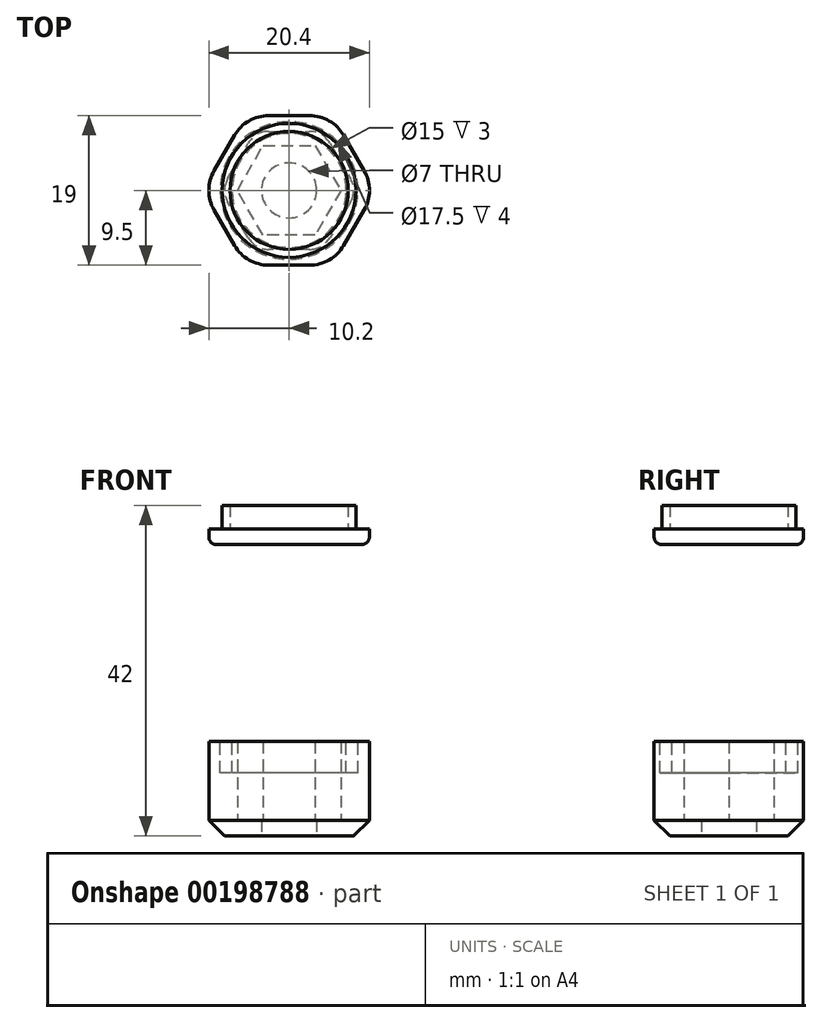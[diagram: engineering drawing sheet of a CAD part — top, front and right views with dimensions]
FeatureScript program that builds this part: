
annotation { "Feature Type Name" : "Feature", "Feature Type Description" : "" }
export const myFeature = defineFeature(function(context is Context, id is Id, definition is map)
    precondition{}
    {
        {
            var Q0;
            Q0=qCreatedBy(makeId("Top.planeOp"),FACE);
            var sketch = newSketch(context, id + "F0", { "sketchPlane" : qUnion([Q0])});
            skCircle(sketch, "E0.cCircle", {"center": v(0, 0) * mm, "radius": 5.7 * mm, "construction": true});
            skLineSegment(sketch, "E0.0", {"start": v(6.58, 0) * mm, "end": v(3.3, -5.7) * mm});
            skLineSegment(sketch, "E0.1", {"start": v(3.3, -5.7) * mm, "end": v(-3.3, -5.7) * mm});
            skLineSegment(sketch, "E0.2", {"start": v(-3.3, -5.7) * mm, "end": v(-6.58, 0) * mm});
            skLineSegment(sketch, "E0.3", {"start": v(-6.58, 0) * mm, "end": v(-3.3, 5.7) * mm});
            skLineSegment(sketch, "E0.4", {"start": v(-3.3, 5.7) * mm, "end": v(3.3, 5.7) * mm});
            skLineSegment(sketch, "E0.5", {"start": v(3.3, 5.7) * mm, "end": v(6.58, 0) * mm});
            skPoint(sketch, "E0.0.midPoint", {"position": v(4.94, -2.85) * mm});
            skCircle(sketch, "E1.cCircle", {"center": v(0, 0) * mm, "radius": 9.5 * mm, "construction": true});
            skLineSegment(sketch, "E1.0", {"start": v(-5.48, 9.5) * mm, "end": v(5.48, 9.5) * mm});
            skLineSegment(sketch, "E1.1", {"start": v(5.48, 9.5) * mm, "end": v(10.97, 0) * mm});
            skLineSegment(sketch, "E1.2", {"start": v(10.97, 0) * mm, "end": v(5.48, -9.5) * mm});
            skLineSegment(sketch, "E1.3", {"start": v(5.48, -9.5) * mm, "end": v(-5.48, -9.5) * mm});
            skLineSegment(sketch, "E1.4", {"start": v(-5.48, -9.5) * mm, "end": v(-10.97, 0) * mm});
            skLineSegment(sketch, "E1.5", {"start": v(-10.97, 0) * mm, "end": v(-5.48, 9.5) * mm});
            skPoint(sketch, "E1.0.midPoint", {"position": v(0, 9.5) * mm});
            skCircle(sketch, "E2", {"center": v(0, 0) * mm, "radius": 3.5 * mm});
            skSolve(sketch);
        }
        {
            var Q0;
            Q0 = qSketchRegion(id + "F0", true);
            extrude(context, id + "F1", {"entities" : qUnion([Q0]), "depth" : 12 * mm});
        }
        {
            var Q0;
            Q0=makeQuery(id+"F0.imprint","IMPRINT",FACE,{"disambiguationData":[TD([[makeQuery(id+"F0.imprint","IMPRINT",EDGE,{"derivedFrom":sQuery(id+"F0.wireOp",EDGE,"E0.0")}),-1.0]])]});
            extrude(context, id + "F2", {"entities" : qUnion([Q0]), "operationType" : NewBodyOperationType.ADD, "depth" : 2 * mm});
        }
        {
            var Q0;
            Q0=makeQuery(id+"F1.opExtrude","SWEPT_EDGE",EDGE,{"disambiguationData":[OSD([sQuery(id+"F0.wireOp",EDGE,"E1.0"),sQuery(id+"F0.wireOp",EDGE,"E1.5")])]});
            var Q1;
            Q1=makeQuery(id+"F1.opExtrude","SWEPT_EDGE",EDGE,{"disambiguationData":[OSD([sQuery(id+"F0.wireOp",EDGE,"E1.4"),sQuery(id+"F0.wireOp",EDGE,"E1.5")])]});
            var Q2;
            Q2=makeQuery(id+"F1.opExtrude","SWEPT_EDGE",EDGE,{"disambiguationData":[OSD([sQuery(id+"F0.wireOp",EDGE,"E1.3"),sQuery(id+"F0.wireOp",EDGE,"E1.4")])]});
            var Q3;
            Q3=makeQuery(id+"F1.opExtrude","SWEPT_EDGE",EDGE,{"disambiguationData":[OSD([sQuery(id+"F0.wireOp",EDGE,"E1.2"),sQuery(id+"F0.wireOp",EDGE,"E1.3")])]});
            var Q4;
            Q4=makeQuery(id+"F1.opExtrude","SWEPT_EDGE",EDGE,{"disambiguationData":[OSD([sQuery(id+"F0.wireOp",EDGE,"E1.1"),sQuery(id+"F0.wireOp",EDGE,"E1.2")])]});
            var Q5;
            Q5=makeQuery(id+"F1.opExtrude","SWEPT_EDGE",EDGE,{"disambiguationData":[OSD([sQuery(id+"F0.wireOp",EDGE,"E1.0"),sQuery(id+"F0.wireOp",EDGE,"E1.1")])]});
            fillet(context, id + "F3", {"entities" : qUnion([Q0, Q1, Q2, Q3, Q4, Q5]), "radius" : 5 * mm, "tangentPropagation" : true, "allowEdgeOverflow" : false});
        }
        {
            var Q0;
            Q0=makeQuery(id+"F1.opExtrude","CAP_FACE",FACE,{"disambiguationData":[OSD([sQuery(id+"F0.wireOp",EDGE,"E0.0"),sQuery(id+"F0.wireOp",EDGE,"E0.1"),sQuery(id+"F0.wireOp",EDGE,"E0.2"),sQuery(id+"F0.wireOp",EDGE,"E0.3"),sQuery(id+"F0.wireOp",EDGE,"E0.4"),sQuery(id+"F0.wireOp",EDGE,"E0.5"),sQuery(id+"F0.wireOp",EDGE,"E1.0"),sQuery(id+"F0.wireOp",EDGE,"E1.1"),sQuery(id+"F0.wireOp",EDGE,"E1.2"),sQuery(id+"F0.wireOp",EDGE,"E1.3"),sQuery(id+"F0.wireOp",EDGE,"E1.4"),sQuery(id+"F0.wireOp",EDGE,"E1.5")])],"isStart":false});
            var sketch = newSketch(context, id + "F4", { "sketchPlane" : qUnion([Q0])});
            skCircle(sketch, "E3", {"center": v(0, 0) * mm, "radius": 7.25 * mm});
            skCircle(sketch, "E4", {"center": v(0, 0) * mm, "radius": 8.75 * mm});
            skSolve(sketch);
        }
        {
            var Q0;
            Q0 = qSketchRegion(id + "F4", true);
            extrude(context, id + "F5", {"entities" : qUnion([Q0]), "operationType" : NewBodyOperationType.REMOVE, "oppositeDirection" : true, "depth" : 4 * mm});
        }
        {
            var Q0;
            {var subQ0=sQuery(id+"F0.wireOp",EDGE,"E1.3");var subQ1=sQuery(id+"F0.wireOp",EDGE,"E1.2");var subQ2=sQuery(id+"F0.wireOp",EDGE,"E1.1");var subQ3=sQuery(id+"F0.wireOp",EDGE,"E1.0");var subQ4=sQuery(id+"F0.wireOp",EDGE,"E1.5");var subQ5=sQuery(id+"F0.wireOp",EDGE,"E1.4");Q0=makeQuery(id+"F5.boolean.opBoolean","SPLIT",FACE,{"disambiguationData":[TD([makeQuery(id+"F1.opExtrude","SWEPT_FACE",FACE,{"disambiguationData":[OSD([subQ3])]})])],"derivedFrom":makeQuery(id+"F1.opExtrude","CAP_FACE",FACE,{"disambiguationData":[OSD([sQuery(id+"F0.wireOp",EDGE,"E0.0"),sQuery(id+"F0.wireOp",EDGE,"E0.1"),sQuery(id+"F0.wireOp",EDGE,"E0.2"),sQuery(id+"F0.wireOp",EDGE,"E0.3"),sQuery(id+"F0.wireOp",EDGE,"E0.4"),sQuery(id+"F0.wireOp",EDGE,"E0.5"),subQ3,subQ2,subQ1,subQ0,subQ5,subQ4])],"isStart":false})});}
            cPlane(context, id + "F6", {"entities" : qUnion([Q0]), "cplaneType" : CPlaneType.OFFSET, "offset" : 25 * mm, "width" : 150 * mm, "height" : 150 * mm});
        }
        {
            var Q0;
            Q0=qCreatedBy(id+"F6.planeOp",FACE);
            var sketch = newSketch(context, id + "F7", { "sketchPlane" : qUnion([Q0])});
            skPoint(sketch, "E5.0", {"position": v(10.2, 0) * mm});
            skLineSegment(sketch, "E6.0", {"start": v(-2.6, 9.5) * mm, "end": v(2.6, 9.5) * mm});
            skArc(sketch, "E7.0", {"start": v(6.93, 7) * mm, "mid": v(5.1, 8.83) * mm, "end": v(2.6, 9.5) * mm});
            skArc(sketch, "E8.0", {"start": v(-2.6, 9.5) * mm, "mid": v(-5.1, 8.83) * mm, "end": v(-6.93, 7) * mm});
            skCircle(sketch, "E9.0", {"center": v(0, 0) * mm, "radius": 9.5 * mm});
            skLineSegment(sketch, "E10.0", {"start": v(-8.23, 4.75) * mm, "end": v(-6.93, 7) * mm});
            skPoint(sketch, "E11.orphan", {"position": v(-10.97, 0) * mm});
            skPoint(sketch, "E12.orphan", {"position": v(-5.48, 9.5) * mm});
            skPoint(sketch, "E13.0.start.orphan", {"position": v(-5.48, -9.5) * mm});
            skPoint(sketch, "E14.0.start.orphan", {"position": v(5.48, -9.5) * mm});
            skPoint(sketch, "E15.0.start.orphan", {"position": v(10.97, 0) * mm});
            skPoint(sketch, "E16.0.start.orphan", {"position": v(5.48, 9.5) * mm});
            skArc(sketch, "E17.0", {"start": v(-9.53, 2.5) * mm, "mid": v(-10.2, 0) * mm, "end": v(-9.53, -2.5) * mm});
            skLineSegment(sketch, "E18.0", {"start": v(-9.53, 2.5) * mm, "end": v(-6.93, 7) * mm});
            skLineSegment(sketch, "E19.0", {"start": v(-6.93, -7) * mm, "end": v(-9.53, -2.5) * mm});
            skArc(sketch, "E20.0", {"start": v(-6.93, -7) * mm, "mid": v(-5.1, -8.83) * mm, "end": v(-2.6, -9.5) * mm});
            skLineSegment(sketch, "E21.0", {"start": v(2.6, -9.5) * mm, "end": v(-2.6, -9.5) * mm});
            skArc(sketch, "E22.0", {"start": v(2.6, -9.5) * mm, "mid": v(5.1, -8.83) * mm, "end": v(6.93, -7) * mm});
            skLineSegment(sketch, "E23.0", {"start": v(9.53, -2.5) * mm, "end": v(8.23, -4.75) * mm});
            skArc(sketch, "E24.0", {"start": v(9.53, -2.5) * mm, "mid": v(10.2, 0) * mm, "end": v(9.53, 2.5) * mm});
            skLineSegment(sketch, "E25.0", {"start": v(6.93, 7) * mm, "end": v(9.53, 2.5) * mm});
            skLineSegment(sketch, "E26.0", {"start": v(9.53, -2.5) * mm, "end": v(6.93, -7) * mm});
            skCircle(sketch, "E27", {"center": v(0, 0) * mm, "radius": 8.5 * mm});
            skCircle(sketch, "E28", {"center": v(0, 0) * mm, "radius": 7.5 * mm});
            skSolve(sketch);
        }
        {
            var Q0;
            Q0=makeQuery(id+"F7.imprint","IMPRINT",FACE,{"disambiguationData":[TD([[makeQuery(id+"F7.imprint","IMPRINT",EDGE,{"derivedFrom":sQuery(id+"F7.wireOp",EDGE,"E27")}),1.0]])]});
            extrude(context, id + "F8", {"entities" : qUnion([Q0]), "depth" : 5 * mm});
        }
        {
            var Q0;
            Q0=makeQuery(id+"F7.imprint","IMPRINT",FACE,{"disambiguationData":[TD([[makeQuery(id+"F7.imprint","IMPRINT",EDGE,{"derivedFrom":sQuery(id+"F7.wireOp",EDGE,"E27")}),1.0]])]});
            var Q1;
            Q1=makeQuery(id+"F7.imprint","IMPRINT",FACE,{"disambiguationData":[TD([[makeQuery(id+"F7.imprint","IMPRINT",EDGE,{"derivedFrom":sQuery(id+"F7.wireOp",EDGE,"E27")}),-1.0]])]});
            var Q2;
            {var subQ5=sQuery(id+"F7.wireOp",EDGE,"E22.0");Q2=makeQuery(id+"F7.imprint","IMPRINT",FACE,{"disambiguationData":[TD([[makeQuery(id+"F7.imprint","IMPRINT",EDGE,{"derivedFrom":subQ5}),1.0]])]});}
            var Q3;
            {var subQ5=sQuery(id+"F7.wireOp",EDGE,"E20.0");Q3=makeQuery(id+"F7.imprint","IMPRINT",FACE,{"disambiguationData":[TD([[makeQuery(id+"F7.imprint","IMPRINT",EDGE,{"derivedFrom":subQ5}),1.0]])]});}
            var Q4;
            {var subQ5=sQuery(id+"F7.wireOp",EDGE,"E17.0");Q4=makeQuery(id+"F7.imprint","IMPRINT",FACE,{"disambiguationData":[TD([[makeQuery(id+"F7.imprint","IMPRINT",EDGE,{"derivedFrom":subQ5}),1.0]])]});}
            var Q5;
            {var subQ0=sQuery(id+"F7.wireOp",EDGE,"E8.0");Q5=makeQuery(id+"F7.imprint","IMPRINT",FACE,{"disambiguationData":[TD([[makeQuery(id+"F7.imprint","IMPRINT",EDGE,{"derivedFrom":subQ0}),1.0]])]});}
            var Q6;
            {var subQ0=sQuery(id+"F7.wireOp",EDGE,"E7.0");Q6=makeQuery(id+"F7.imprint","IMPRINT",FACE,{"disambiguationData":[TD([[makeQuery(id+"F7.imprint","IMPRINT",EDGE,{"derivedFrom":subQ0}),1.0]])]});}
            var Q7;
            Q7=makeQuery(id+"F7.imprint","IMPRINT",FACE,{"disambiguationData":[TD([[makeQuery(id+"F7.imprint","IMPRINT",EDGE,{"derivedFrom":sQuery(id+"F7.wireOp",EDGE,"E28")}),1.0]])]});
            var Q8;
            {var subQ5=sQuery(id+"F7.wireOp",EDGE,"E24.0");Q8=makeQuery(id+"F7.imprint","IMPRINT",FACE,{"disambiguationData":[TD([[makeQuery(id+"F7.imprint","IMPRINT",EDGE,{"derivedFrom":subQ5}),1.0]])]});}
            extrude(context, id + "F9", {"entities" : qUnion([Q0, Q1, Q2, Q3, Q4, Q5, Q6, Q7, Q8]), "operationType" : NewBodyOperationType.ADD, "depth" : 2 * mm});
        }
        {
            var Q0;
            Q0=makeQuery(id+"F9.boolean.opBoolean","MERGE",FACE,{"derivedFrom":[makeQuery(id+"F8.opExtrude","CAP_FACE",FACE,{"disambiguationData":[OSD([sQuery(id+"F7.wireOp",EDGE,"E27"),sQuery(id+"F7.wireOp",EDGE,"E28")])],"isStart":true}),makeQuery(id+"F9.opExtrude","CAP_FACE",FACE,{"disambiguationData":[OSD([sQuery(id+"F7.wireOp",EDGE,"E6.0"),sQuery(id+"F7.wireOp",EDGE,"E7.0"),sQuery(id+"F7.wireOp",EDGE,"E8.0"),sQuery(id+"F7.wireOp",EDGE,"E9.0"),sQuery(id+"F7.wireOp",EDGE,"E17.0"),sQuery(id+"F7.wireOp",EDGE,"E18.0"),sQuery(id+"F7.wireOp",EDGE,"E19.0"),sQuery(id+"F7.wireOp",EDGE,"E20.0"),sQuery(id+"F7.wireOp",EDGE,"E21.0"),sQuery(id+"F7.wireOp",EDGE,"E22.0"),sQuery(id+"F7.wireOp",EDGE,"E25.0"),sQuery(id+"F7.wireOp",EDGE,"E26.0")])],"isStart":true})]});
            fillet(context, id + "F10", {"entities" : qUnion([Q0]), "radius" : 1 * mm, "tangentPropagation" : true, "allowEdgeOverflow" : false});
        }
        {
            var Q0;
            Q0=makeQuery(id+"F1.opExtrude","CAP_EDGE",EDGE,{"disambiguationData":[OSD([sQuery(id+"F0.wireOp",EDGE,"E1.0")])],"isStart":true});
            var Q1;
            {var subQ0=sQuery(id+"F0.wireOp",EDGE,"E0.5");var subQ1=sQuery(id+"F0.wireOp",EDGE,"E0.4");var subQ2=sQuery(id+"F0.wireOp",EDGE,"E0.3");var subQ3=sQuery(id+"F0.wireOp",EDGE,"E0.2");var subQ4=sQuery(id+"F0.wireOp",EDGE,"E0.1");var subQ5=sQuery(id+"F0.wireOp",EDGE,"E0.0");var subQ6=sQuery(id+"F0.wireOp",EDGE,"E1.1");var subQ7=sQuery(id+"F0.wireOp",EDGE,"E1.0");Q1=makeQuery(id+"F3.opFillet","BLEND_EDGE",EDGE,{"blendedFrom":[makeQuery(id+"F1.opExtrude","SWEPT_EDGE",EDGE,{"disambiguationData":[OSD([subQ7,subQ6])]}),makeQuery(id+"F2.boolean.opBoolean","MERGE",FACE,{"derivedFrom":[makeQuery(id+"F1.opExtrude","CAP_FACE",FACE,{"disambiguationData":[OSD([subQ5,subQ4,subQ3,subQ2,subQ1,subQ0,subQ7,subQ6,sQuery(id+"F0.wireOp",EDGE,"E1.2"),sQuery(id+"F0.wireOp",EDGE,"E1.3"),sQuery(id+"F0.wireOp",EDGE,"E1.4"),sQuery(id+"F0.wireOp",EDGE,"E1.5")])],"isStart":true}),makeQuery(id+"F2.opExtrude","CAP_FACE",FACE,{"disambiguationData":[OSD([subQ5,subQ4,subQ3,subQ2,subQ1,subQ0,sQuery(id+"F0.wireOp",EDGE,"E2")])],"isStart":true})]})],"blendedInto":[makeQuery(id+"F2.boolean.opBoolean","MERGE",FACE,{"derivedFrom":[makeQuery(id+"F1.opExtrude","CAP_FACE",FACE,{"disambiguationData":[OSD([subQ5,subQ4,subQ3,subQ2,subQ1,subQ0,subQ7,subQ6,sQuery(id+"F0.wireOp",EDGE,"E1.2"),sQuery(id+"F0.wireOp",EDGE,"E1.3"),sQuery(id+"F0.wireOp",EDGE,"E1.4"),sQuery(id+"F0.wireOp",EDGE,"E1.5")])],"isStart":true}),makeQuery(id+"F2.opExtrude","CAP_FACE",FACE,{"disambiguationData":[OSD([subQ5,subQ4,subQ3,subQ2,subQ1,subQ0,sQuery(id+"F0.wireOp",EDGE,"E2")])],"isStart":true})]})]});}
            chamfer(context, id + "F11", {"entities" : qUnion([Q0, Q1]), "width" : 2 * mm, "tangentPropagation" : true});
        }
    });
